# Revit family: SW06 STERN
name_source: partatom
category: Detail Items
units: mm (PartAtom-declared; Revit-internal decimal feet)

## family parameters
Rotate with component = No
Section Shape = Not Defined
Shared = No

## types (6) — shared parameters
URL = www.superwood.dk

## per-type parameters (varying)
| type | Mellemstern | Overstern | Understern | h |
| SW06 STERN UNDER - 21x120mm | No | No | Yes | 120 mm  [stored 0.393701 ft] |
| SW06 STERN UNDER - 21x145mm | No | No | Yes | 145 mm  [stored 0.475722 ft] |
| SW06 STERN OVER - 21x120mm | No | Yes | No | 120 mm  [stored 0.393701 ft] |
| SW06 STERN OVER - 21x145mm | No | Yes | No | 145 mm  [stored 0.475722 ft] |
| SW06 STERN MELLEM - 21x145mm | Yes | No | No | 145 mm  [stored 0.475722 ft] |
| SW06 STERN MELLEM - 21x120mm | Yes | No | No | 120 mm  [stored 0.393701 ft] |

note: [stored X ft] marks values corroborated as IEEE doubles in the binary element streams (Revit-internal decimal feet)

## geometry (parser evidence)
native form markers: Sweep x6
no freeform markers — native parametric forms only
